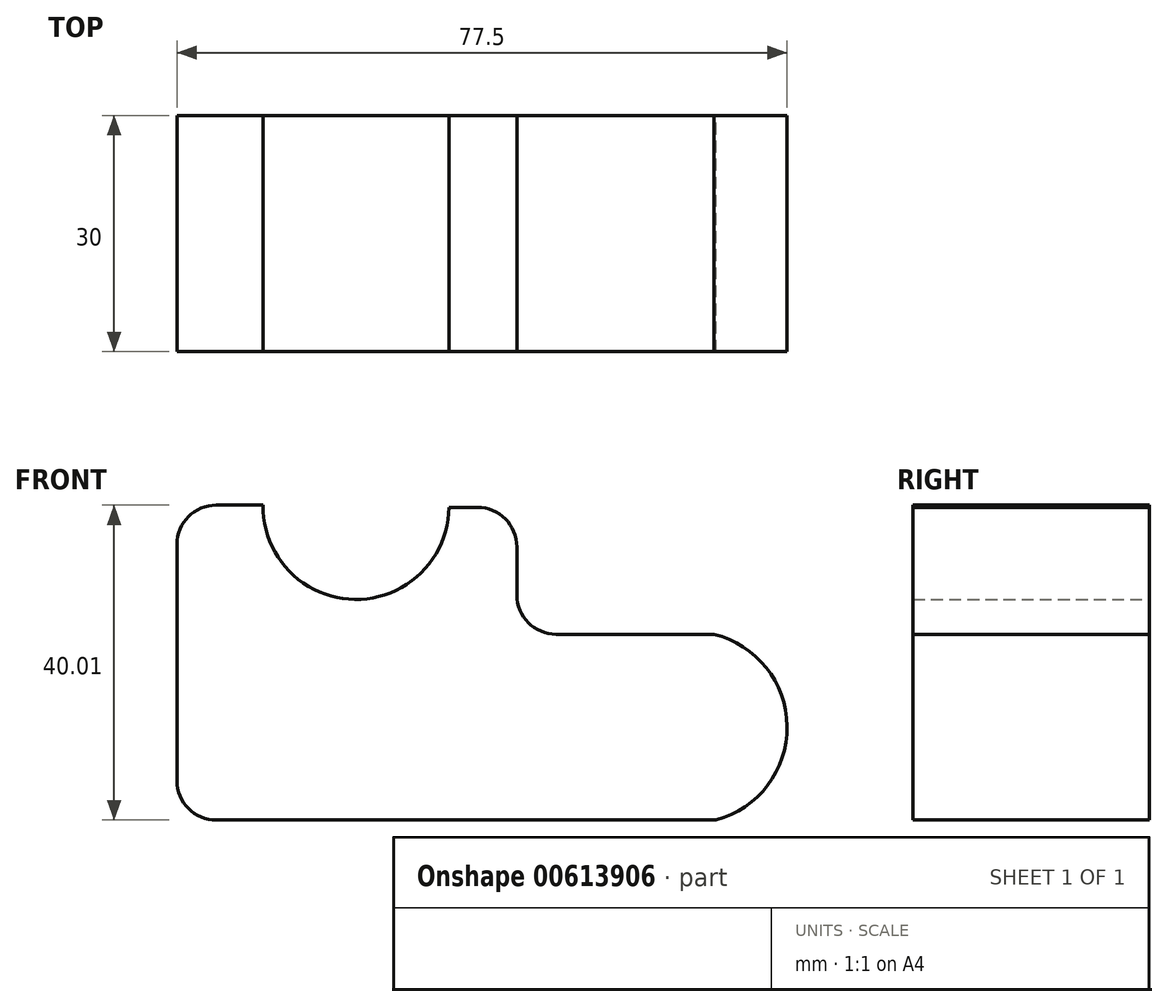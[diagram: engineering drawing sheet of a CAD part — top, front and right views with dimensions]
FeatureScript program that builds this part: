
annotation { "Feature Type Name" : "Feature", "Feature Type Description" : "" }
export const myFeature = defineFeature(function(context is Context, id is Id, definition is map)
    precondition{}
    {
        {
            var Q0;
            Q0=qCreatedBy(makeId("Front.planeOp"),FACE);
            var sketch = newSketch(context, id + "F0", { "sketchPlane" : qUnion([Q0])});
            skLineSegment(sketch, "E0", {"start": v(-64.32, 43.2) * mm, "end": v(-64.32, 13.2) * mm});
            skLineSegment(sketch, "E1", {"start": v(-59.32, 8.2) * mm, "end": v(4.17, 8.2) * mm});
            skLineSegment(sketch, "E2", {"start": v(-59.32, 48.2) * mm, "end": v(-53.39, 48.2) * mm});
            skLineSegment(sketch, "E3", {"start": v(-29.79, 47.92) * mm, "end": v(-26.15, 47.92) * mm});
            skLineSegment(sketch, "E4", {"start": v(-21.15, 42.92) * mm, "end": v(-21.15, 36.8) * mm});
            skLineSegment(sketch, "E5", {"start": v(-16.15, 31.8) * mm, "end": v(3.89, 31.8) * mm});
            skArc(sketch, "E6", {"start": v(-53.39, 48.2) * mm, "mid": v(-41.73, 36.24) * mm, "end": v(-29.79, 47.92) * mm});
            skArc(sketch, "E7", {"start": v(4.17, 8.2) * mm, "mid": v(13.18, 20.11) * mm, "end": v(3.89, 31.8) * mm});
            skPoint(sketch, "E8.visualSharp", {"position": v(-64.32, 48.2) * mm});
            skArc(sketch, "E8.filletArc", {"start": v(-59.32, 48.2) * mm, "mid": v(-62.86, 46.74) * mm, "end": v(-64.32, 43.2) * mm});
            skPoint(sketch, "E9.visualSharp", {"position": v(-21.15, 47.92) * mm});
            skArc(sketch, "E9.filletArc", {"start": v(-21.15, 42.92) * mm, "mid": v(-22.62, 46.46) * mm, "end": v(-26.15, 47.92) * mm});
            skPoint(sketch, "E10.visualSharp", {"position": v(-21.15, 31.8) * mm});
            skArc(sketch, "E10.filletArc", {"start": v(-21.15, 36.8) * mm, "mid": v(-19.69, 33.27) * mm, "end": v(-16.15, 31.8) * mm});
            skPoint(sketch, "E11.visualSharp", {"position": v(-64.32, 8.2) * mm});
            skArc(sketch, "E11.filletArc", {"start": v(-64.32, 13.2) * mm, "mid": v(-62.86, 9.67) * mm, "end": v(-59.32, 8.2) * mm});
            skSolve(sketch);
        }
        {
            var Q0;
            Q0 = qSketchRegion(id + "F0", true);
            extrude(context, id + "F1", {"entities" : qUnion([Q0]), "depth" : 30 * mm, "offsetDistance" : 25 * mm});
        }
    });
